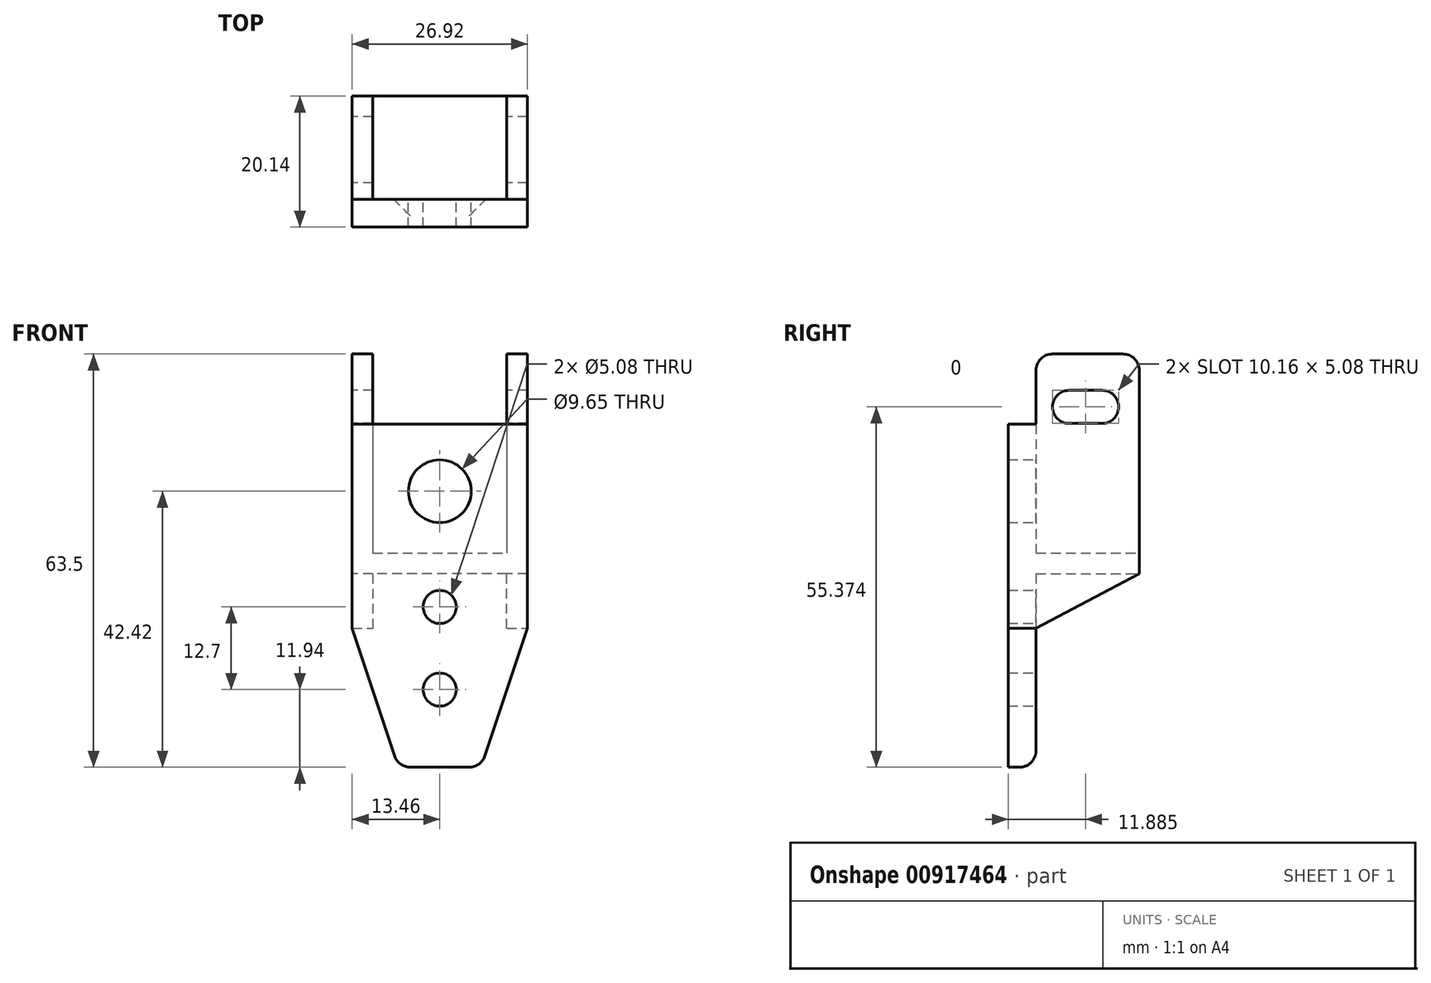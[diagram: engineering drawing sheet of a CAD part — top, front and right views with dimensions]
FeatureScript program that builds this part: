
annotation { "Feature Type Name" : "Feature", "Feature Type Description" : "" }
export const myFeature = defineFeature(function(context is Context, id is Id, definition is map)
    precondition{}
    {
        {
            var Q0;
            Q0=qCreatedBy(makeId("Front.planeOp"),FACE);
            var sketch = newSketch(context, id + "F0", { "sketchPlane" : qUnion([Q0])});
            skLineSegment(sketch, "E0", {"start": v(0, 56.06) * mm, "end": v(0, -49.98) * mm, "construction": true});
            skLineSegment(sketch, "E1", {"start": v(-13.46, 33.78) * mm, "end": v(-13.46, -8.38) * mm});
            skLineSegment(sketch, "E2", {"start": v(13.46, 33.78) * mm, "end": v(13.46, -8.38) * mm});
            skLineSegment(sketch, "E3", {"start": v(0, 0) * mm, "end": v(-13.46, 0) * mm});
            skLineSegment(sketch, "E4", {"start": v(0, 0) * mm, "end": v(13.46, 0) * mm});
            skLineSegment(sketch, "E5.0", {"start": v(-10.29, 33.78) * mm, "end": v(-10.29, -8.38) * mm});
            skLineSegment(sketch, "E6.0", {"start": v(10.29, 33.78) * mm, "end": v(10.29, -8.38) * mm});
            skLineSegment(sketch, "E7.0", {"start": v(0, 3.18) * mm, "end": v(-13.46, 3.18) * mm});
            skLineSegment(sketch, "E7.1", {"start": v(0, 3.18) * mm, "end": v(13.46, 3.18) * mm});
            skLineSegment(sketch, "E8", {"start": v(-13.46, 33.78) * mm, "end": v(-10.29, 33.78) * mm});
            skLineSegment(sketch, "E9", {"start": v(-13.46, -8.38) * mm, "end": v(-10.29, -8.38) * mm});
            skLineSegment(sketch, "E10", {"start": v(10.29, -8.38) * mm, "end": v(13.46, -8.38) * mm});
            skLineSegment(sketch, "E11", {"start": v(10.29, 33.78) * mm, "end": v(13.46, 33.78) * mm});
            skPoint(sketch, "E12", {"position": v(0, -29.72) * mm});
            skSolve(sketch);
        }
        {
            var Q0;
            {var subQ0=sQuery(id+"F0.wireOp",EDGE,"E9");Q0=makeQuery(id+"F0.imprint","IMPRINT",FACE,{"disambiguationData":[TD([[makeQuery(id+"F0.imprint","IMPRINT",EDGE,{"derivedFrom":subQ0}),1.0]])]});}
            var Q1;
            {var subQ1=sQuery(id+"F0.wireOp",EDGE,"E4");var subQ5=sQuery(id+"F0.wireOp",EDGE,"E3");var subQ6=makeQuery(id+"F0.imprint","INTERSECT",VERTEX,{"derivedFrom":[subQ5,subQ1]});Q1=makeQuery(id+"F0.imprint","IMPRINT",FACE,{"disambiguationData":[TD([[makeQuery(id+"F0.imprint","IMPRINT",EDGE,{"disambiguationData":[TD([[subQ6,-1.0]])],"derivedFrom":subQ5}),-1.0]])]});}
            var Q2;
            {var subQ0=sQuery(id+"F0.wireOp",EDGE,"E8");Q2=makeQuery(id+"F0.imprint","IMPRINT",FACE,{"disambiguationData":[TD([[makeQuery(id+"F0.imprint","IMPRINT",EDGE,{"derivedFrom":subQ0}),-1.0]])]});}
            var Q3;
            {var subQ0=sQuery(id+"F0.wireOp",EDGE,"E10");Q3=makeQuery(id+"F0.imprint","IMPRINT",FACE,{"disambiguationData":[TD([[makeQuery(id+"F0.imprint","IMPRINT",EDGE,{"derivedFrom":subQ0}),1.0]])]});}
            var Q4;
            {var subQ0=sQuery(id+"F0.wireOp",EDGE,"E3");var subQ1=sQuery(id+"F0.wireOp",EDGE,"E1");var subQ2=makeQuery(id+"F0.imprint","INTERSECT",VERTEX,{"derivedFrom":[subQ1,subQ0]});Q4=makeQuery(id+"F0.imprint","IMPRINT",FACE,{"disambiguationData":[TD([[makeQuery(id+"F0.imprint","IMPRINT",EDGE,{"disambiguationData":[TD([[subQ2,1.0]])],"derivedFrom":subQ1}),1.0]])]});}
            var Q5;
            {var subQ0=sQuery(id+"F0.wireOp",EDGE,"E11");Q5=makeQuery(id+"F0.imprint","IMPRINT",FACE,{"disambiguationData":[TD([[makeQuery(id+"F0.imprint","IMPRINT",EDGE,{"derivedFrom":subQ0}),-1.0]])]});}
            var Q6;
            {var subQ0=sQuery(id+"F0.wireOp",EDGE,"E4");var subQ1=sQuery(id+"F0.wireOp",EDGE,"E2");var subQ2=makeQuery(id+"F0.imprint","INTERSECT",VERTEX,{"derivedFrom":[subQ1,subQ0]});Q6=makeQuery(id+"F0.imprint","IMPRINT",FACE,{"disambiguationData":[TD([[makeQuery(id+"F0.imprint","IMPRINT",EDGE,{"disambiguationData":[TD([[subQ2,1.0]])],"derivedFrom":subQ1}),-1.0]])]});}
            extrude(context, id + "F1", {"entities" : qUnion([Q0, Q1, Q2, Q3, Q4, Q5, Q6]), "depth" : 15.88 * mm, "offsetDistance" : 25.4 * mm});
        }
        {
            var Q0;
            Q0=makeQuery(id+"F1.opExtrude","CAP_FACE",FACE,{"disambiguationData":[OSD([sQuery(id+"F0.wireOp",EDGE,"E1"),sQuery(id+"F0.wireOp",EDGE,"E2"),sQuery(id+"F0.wireOp",EDGE,"E3"),sQuery(id+"F0.wireOp",EDGE,"E4"),sQuery(id+"F0.wireOp",EDGE,"E5.0"),sQuery(id+"F0.wireOp",EDGE,"E6.0"),sQuery(id+"F0.wireOp",EDGE,"E7.0"),sQuery(id+"F0.wireOp",EDGE,"E7.1"),sQuery(id+"F0.wireOp",EDGE,"E8"),sQuery(id+"F0.wireOp",EDGE,"E9"),sQuery(id+"F0.wireOp",EDGE,"E10"),sQuery(id+"F0.wireOp",EDGE,"E11")])],"isStart":false});
            var sketch = newSketch(context, id + "F2", { "sketchPlane" : qUnion([Q0])});
            skLineSegment(sketch, "E13", {"start": v(-13.46, 22.99) * mm, "end": v(13.46, 22.99) * mm});
            skLineSegment(sketch, "E14", {"start": v(13.46, 22.99) * mm, "end": v(13.46, -8.38) * mm});
            skLineSegment(sketch, "E15", {"start": v(-13.46, 22.99) * mm, "end": v(-13.46, -8.38) * mm});
            skPoint(sketch, "E16", {"position": v(0, -29.72) * mm});
            skLineSegment(sketch, "E17", {"start": v(-6.35, -29.72) * mm, "end": v(6.35, -29.72) * mm});
            skLineSegment(sketch, "E18", {"start": v(-13.46, -8.38) * mm, "end": v(-6.35, -29.72) * mm});
            skLineSegment(sketch, "E19", {"start": v(13.46, -8.38) * mm, "end": v(6.35, -29.72) * mm});
            skCircle(sketch, "E20", {"center": v(0, -5.08) * mm, "radius": 2.54 * mm});
            skCircle(sketch, "E21", {"center": v(0, -17.78) * mm, "radius": 2.54 * mm});
            skCircle(sketch, "E22", {"center": v(0, 12.7) * mm, "radius": 4.83 * mm});
            skPoint(sketch, "E22.centerSnap0", {"position": v(0, 3.18) * mm});
            skPoint(sketch, "E22.centerSnap1", {"position": v(-13.46, 12.7) * mm});
            skSolve(sketch);
        }
        {
            var Q0;
            Q0=makeQuery(id+"F2.imprint","IMPRINT",FACE,{"disambiguationData":[TD([[makeQuery(id+"F2.imprint","IMPRINT",EDGE,{"derivedFrom":sQuery(id+"F2.wireOp",EDGE,"458P89qb-jg9T-EiMf-0dZx-tcgOWhvGFjyi")}),1.0]])]});
            var Q1;
            {var subQ2=sQuery(id+"F0.wireOp",EDGE,"E7.0");var subQ6=sQuery(id+"F0.wireOp",EDGE,"E7.1");var subQ9=makeQuery(id+"F1.opExtrude","CAP_EDGE",EDGE,{"disambiguationData":[OSD([subQ2,subQ6])],"isStart":false});Q1=makeQuery(id+"F2.imprint","IMPRINT",FACE,{"disambiguationData":[TD([[makeQuery(id+"F2.imprint","IMPRINT",EDGE,{"derivedFrom":subQ9}),1.0]])]});}
            var Q2;
            {var subQ13=sQuery(id+"F2.wireOp",EDGE,"E14");Q2=makeQuery(id+"F2.imprint","IMPRINT",FACE,{"disambiguationData":[TD([[makeQuery(id+"F2.imprint","IMPRINT",EDGE,{"derivedFrom":subQ13}),-1.0]])]});}
            var Q3;
            Q3=makeQuery(id+"F2.imprint","IMPRINT",FACE,{"disambiguationData":[TD([[makeQuery(id+"F2.imprint","IMPRINT",EDGE,{"derivedFrom":sQuery(id+"F2.wireOp",EDGE,"E17")}),1.0]])]});
            var Q4;
            Q4=sQuery(id+"F2.wireOp",EDGE,"E13");
            var Q5;
            Q5=sQuery(id+"F2.wireOp",EDGE,"E15");
            var Q6;
            Q6=sQuery(id+"F2.wireOp",EDGE,"458P89qb-jg9T-EiMf-0dZx-tcgOWhvGFjyi");
            var Q7;
            Q7=sQuery(id+"F2.wireOp",EDGE,"E14");
            extrude(context, id + "F3", {"entities" : qUnion([Q0, Q1, Q2, Q3]), "operationType" : NewBodyOperationType.ADD, "surfaceEntities" : qUnion([Q4, Q5, Q6, Q7]), "depth" : 4.27 * mm, "offsetDistance" : 25.4 * mm});
        }
        {
            var Q0;
            Q0=makeQuery(id+"F3.boolean.opBoolean","MERGE",FACE,{"derivedFrom":[makeQuery(id+"F1.opExtrude","SWEPT_FACE",FACE,{"disambiguationData":[OSD([sQuery(id+"F0.wireOp",EDGE,"E1")])]}),makeQuery(id+"F3.opExtrude","SWEPT_FACE",FACE,{"disambiguationData":[OSD([sQuery(id+"F2.wireOp",EDGE,"E15")])]})]});
            var sketch = newSketch(context, id + "F4", { "sketchPlane" : qUnion([Q0])});
            skCircle(sketch, "E23", {"center": v(10.8, 25.65) * mm, "radius": 2.54 * mm});
            skCircle(sketch, "E24", {"center": v(5.71, 25.65) * mm, "radius": 2.54 * mm});
            skLineSegment(sketch, "E25", {"start": v(5.71, 28.2) * mm, "end": v(10.8, 28.2) * mm});
            skLineSegment(sketch, "E26", {"start": v(5.71, 23.11) * mm, "end": v(10.8, 23.11) * mm});
            skLineSegment(sketch, "E27", {"start": v(0, 0) * mm, "end": v(15.88, -8.38) * mm});
            skSolve(sketch);
        }
        {
            var Q0;
            {var subQ0=sQuery(id+"F4.wireOp",EDGE,"E27");Q0=makeQuery(id+"F4.imprint","IMPRINT",FACE,{"disambiguationData":[TD([[makeQuery(id+"F4.imprint","IMPRINT",EDGE,{"derivedFrom":subQ0}),-1.0]])]});}
            var Q1;
            {var subQ0=sQuery(id+"F4.wireOp",EDGE,"E24");var subQ1=makeQuery(id+"F4.imprint","INTERSECT",VERTEX,{"derivedFrom":[subQ0,sQuery(id+"F4.wireOp",EDGE,"E25")]});Q1=makeQuery(id+"F4.imprint","IMPRINT",FACE,{"disambiguationData":[TD([[makeQuery(id+"F4.imprint","IMPRINT",EDGE,{"disambiguationData":[TD([[subQ1,-1.0]])],"derivedFrom":subQ0}),1.0]])]});}
            var Q2;
            {var subQ0=sQuery(id+"F4.wireOp",EDGE,"E25");Q2=makeQuery(id+"F4.imprint","IMPRINT",FACE,{"disambiguationData":[TD([[makeQuery(id+"F4.imprint","IMPRINT",EDGE,{"derivedFrom":subQ0}),-1.0]])]});}
            var Q3;
            {var subQ0=sQuery(id+"F4.wireOp",EDGE,"E23");var subQ1=makeQuery(id+"F4.imprint","INTERSECT",VERTEX,{"derivedFrom":[subQ0,sQuery(id+"F4.wireOp",EDGE,"E25")]});Q3=makeQuery(id+"F4.imprint","IMPRINT",FACE,{"disambiguationData":[TD([[makeQuery(id+"F4.imprint","IMPRINT",EDGE,{"disambiguationData":[TD([[subQ1,-1.0]])],"derivedFrom":subQ0}),1.0]])]});}
            var Q4;
            {var subQ0=sQuery(id+"F4.wireOp",EDGE,"E26");Q4=makeQuery(id+"F4.imprint","IMPRINT",FACE,{"disambiguationData":[TD([[makeQuery(id+"F4.imprint","IMPRINT",EDGE,{"derivedFrom":subQ0}),1.0]])]});}
            extrude(context, id + "F5", {"entities" : qUnion([Q0, Q1, Q2, Q3, Q4]), "operationType" : NewBodyOperationType.REMOVE, "endBound" : BoundingType.THROUGH_ALL, "oppositeDirection" : true, "depth" : 25.4 * mm, "offsetDistance" : 25.4 * mm});
        }
        {
            var Q0;
            Q0=makeQuery(id+"F1.opExtrude","CAP_EDGE",EDGE,{"disambiguationData":[OSD([sQuery(id+"F0.wireOp",EDGE,"E11")])],"isStart":true});
            var Q1;
            Q1=makeQuery(id+"F1.opExtrude","CAP_EDGE",EDGE,{"disambiguationData":[OSD([sQuery(id+"F0.wireOp",EDGE,"E8")])],"isStart":true});
            var Q2;
            Q2=makeQuery(id+"F1.opExtrude","CAP_EDGE",EDGE,{"disambiguationData":[OSD([sQuery(id+"F0.wireOp",EDGE,"E11")])],"isStart":false});
            var Q3;
            Q3=makeQuery(id+"F1.opExtrude","CAP_EDGE",EDGE,{"disambiguationData":[OSD([sQuery(id+"F0.wireOp",EDGE,"E8")])],"isStart":false});
            var Q4;
            {var subQ4=sQuery(id+"F0.wireOp",EDGE,"E1");var subQ5=sQuery(id+"F4.wireOp",EDGE,"E27");Q4=makeQuery(id+"F5.boolean.opBoolean","COPY",EDGE,{"disambiguationData":[TD([makeQuery(id+"F1.opExtrude","SWEPT_FACE",FACE,{"disambiguationData":[OSD([subQ4])]})])],"derivedFrom":makeQuery(id+"F5.opExtrude","SWEPT_EDGE",EDGE,{"disambiguationData":[OSD([subQ4,subQ5])]})});}
            var Q5;
            Q5=makeQuery(id+"F3.opExtrude","SWEPT_EDGE",EDGE,{"disambiguationData":[OSD([sQuery(id+"F2.wireOp",EDGE,"E17"),sQuery(id+"F2.wireOp",EDGE,"E18")])]});
            var Q6;
            Q6=makeQuery(id+"F3.opExtrude","SWEPT_EDGE",EDGE,{"disambiguationData":[OSD([sQuery(id+"F2.wireOp",EDGE,"E17"),sQuery(id+"F2.wireOp",EDGE,"E19")])]});
            var Q7;
            Q7=makeQuery(id+"F3.opExtrude","CAP_EDGE",EDGE,{"disambiguationData":[OSD([sQuery(id+"F2.wireOp",EDGE,"E17")])],"isStart":true});
            fillet(context, id + "F6", {"entities" : qUnion([Q0, Q1, Q2, Q3, Q4, Q5, Q6, Q7]), "radius" : 2.54 * mm, "tangentPropagation" : true, "allowEdgeOverflow" : false});
        }
    });
